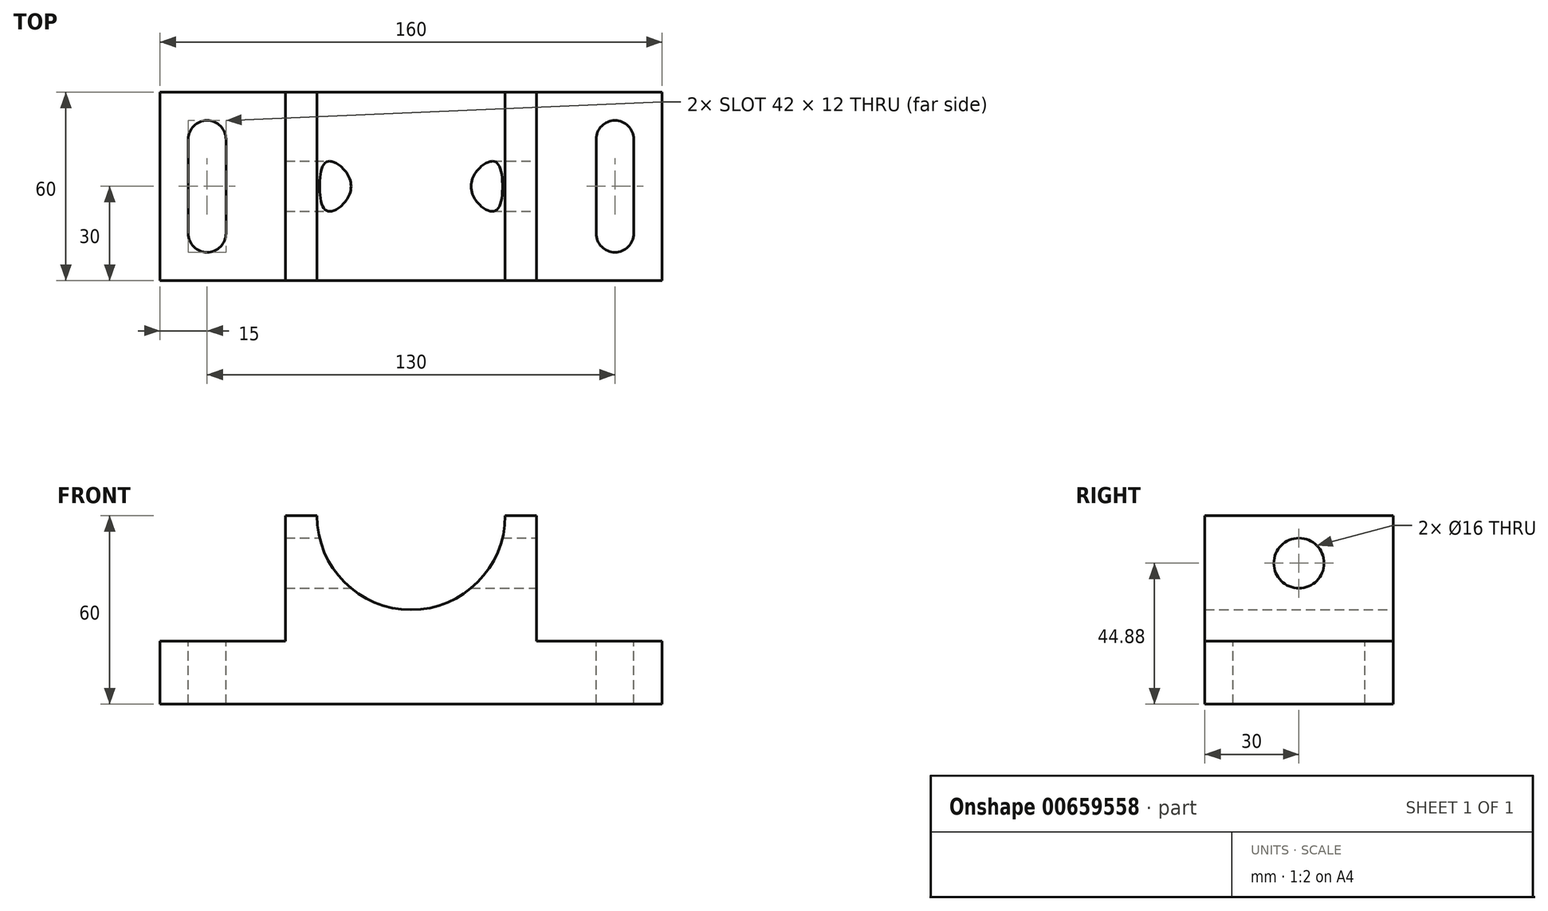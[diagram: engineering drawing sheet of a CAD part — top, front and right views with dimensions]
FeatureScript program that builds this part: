
annotation { "Feature Type Name" : "Feature", "Feature Type Description" : "" }
export const myFeature = defineFeature(function(context is Context, id is Id, definition is map)
    precondition{}
    {
        {
            var Q0;
            Q0=qCreatedBy(makeId("Front.planeOp"),FACE);
            var sketch = newSketch(context, id + "F0", { "sketchPlane" : qUnion([Q0])});
            skLineSegment(sketch, "E0.bottom", {"start": v(-80, -30) * mm, "end": v(80, -30) * mm});
            skLineSegment(sketch, "E0.top", {"start": v(-40, 30) * mm, "end": v(-30, 30) * mm});
            skLineSegment(sketch, "E0.left", {"start": v(-80, -30) * mm, "end": v(-80, -10) * mm});
            skLineSegment(sketch, "E0.right", {"start": v(80, -30) * mm, "end": v(80, -10) * mm});
            skPoint(sketch, "E0.middle", {"position": v(0, 0) * mm});
            skLineSegment(sketch, "E1", {"start": v(-80, -10) * mm, "end": v(-40, -10) * mm});
            skLineSegment(sketch, "E2", {"start": v(-40, -10) * mm, "end": v(-40, 30) * mm});
            skLineSegment(sketch, "E3", {"start": v(80, -10) * mm, "end": v(40, -10) * mm});
            skLineSegment(sketch, "E4", {"start": v(40, -10) * mm, "end": v(40, 30) * mm});
            skPoint(sketch, "E5.orphan", {"position": v(-80, 30) * mm});
            skPoint(sketch, "E6.orphan", {"position": v(80, 30) * mm});
            skArc(sketch, "E7", {"start": v(-30, 30) * mm, "mid": v(0, 0) * mm, "end": v(30, 30) * mm});
            skLineSegment(sketch, "E8.trimOffspring", {"start": v(30, 30) * mm, "end": v(40, 30) * mm});
            skSolve(sketch);
        }
        {
            var Q0;
            Q0 = qSketchRegion(id + "F0", true);
            extrude(context, id + "F1", {"entities" : qUnion([Q0]), "depth" : 60 * mm, "offsetDistance" : 25.4 * mm});
        }
        {
            var Q0;
            Q0=makeQuery(id+"F1.opExtrude","SWEPT_FACE",FACE,{"disambiguationData":[OSD([sQuery(id+"F0.wireOp",EDGE,"E4")])]});
            var sketch = newSketch(context, id + "F2", { "sketchPlane" : qUnion([Q0])});
            skLineSegment(sketch, "E9", {"start": v(-30, -30.12) * mm, "end": v(-30, 14.88) * mm});
            skPoint(sketch, "E9.startSnap0", {"position": v(-30, -10) * mm});
            skCircle(sketch, "E10", {"center": v(-30, 14.88) * mm, "radius": 8 * mm});
            skSolve(sketch);
        }
        {
            var Q0;
            Q0 = qSketchRegion(id + "F2", true);
            extrude(context, id + "F3", {"entities" : qUnion([Q0]), "operationType" : NewBodyOperationType.REMOVE, "endBound" : BoundingType.THROUGH_ALL, "oppositeDirection" : true, "depth" : 25.4 * mm, "offsetDistance" : 25.4 * mm});
        }
        {
            var Q0;
            Q0=makeQuery(id+"F1.opExtrude","SWEPT_FACE",FACE,{"disambiguationData":[OSD([sQuery(id+"F0.wireOp",EDGE,"E1")])]});
            var sketch = newSketch(context, id + "F4", { "sketchPlane" : qUnion([Q0])});
            skLineSegment(sketch, "E11", {"start": v(-80, -60) * mm, "end": v(-65, -60) * mm});
            skLineSegment(sketch, "E12", {"start": v(-65, -60) * mm, "end": v(65, -60) * mm});
            skLineSegment(sketch, "E13", {"start": v(65, -60) * mm, "end": v(80, -60) * mm});
            skLineSegment(sketch, "E14", {"start": v(-65, -60) * mm, "end": v(-65, -45) * mm});
            skLineSegment(sketch, "E15", {"start": v(65, -60) * mm, "end": v(65, -45) * mm});
            skLineSegment(sketch, "E16", {"start": v(-65, -45) * mm, "end": v(-65, -30) * mm});
            skLineSegment(sketch, "E17.bottom", {"start": v(-71, -45) * mm, "end": v(-59, -45) * mm});
            skLineSegment(sketch, "E17.top", {"start": v(-71, -15) * mm, "end": v(-59, -15) * mm});
            skLineSegment(sketch, "E17.left", {"start": v(-71, -45) * mm, "end": v(-71, -15) * mm});
            skLineSegment(sketch, "E17.right", {"start": v(-59, -45) * mm, "end": v(-59, -15) * mm});
            skPoint(sketch, "E17.middle", {"position": v(-65, -30) * mm});
            skCircle(sketch, "E18", {"center": v(-65, -15) * mm, "radius": 6 * mm});
            skLineSegment(sketch, "E19", {"start": v(65, -45) * mm, "end": v(65, -30) * mm});
            skLineSegment(sketch, "E20.bottom", {"start": v(59, -45) * mm, "end": v(71, -45) * mm});
            skLineSegment(sketch, "E20.top", {"start": v(59, -15) * mm, "end": v(71, -15) * mm});
            skLineSegment(sketch, "E20.left", {"start": v(59, -45) * mm, "end": v(59, -15) * mm});
            skLineSegment(sketch, "E20.right", {"start": v(71, -45) * mm, "end": v(71, -15) * mm});
            skPoint(sketch, "E20.middle", {"position": v(65, -30) * mm});
            skCircle(sketch, "E21", {"center": v(65, -15) * mm, "radius": 6 * mm});
            skCircle(sketch, "E22", {"center": v(-65, -45) * mm, "radius": 6 * mm});
            skCircle(sketch, "E23", {"center": v(65, -45) * mm, "radius": 6 * mm});
            skSolve(sketch);
        }
        {
            var Q0;
            Q0 = qSketchRegion(id + "F4", true);
            extrude(context, id + "F5", {"entities" : qUnion([Q0]), "operationType" : NewBodyOperationType.REMOVE, "endBound" : BoundingType.THROUGH_ALL, "oppositeDirection" : true, "depth" : 25.4 * mm, "offsetDistance" : 25.4 * mm});
        }
    });
